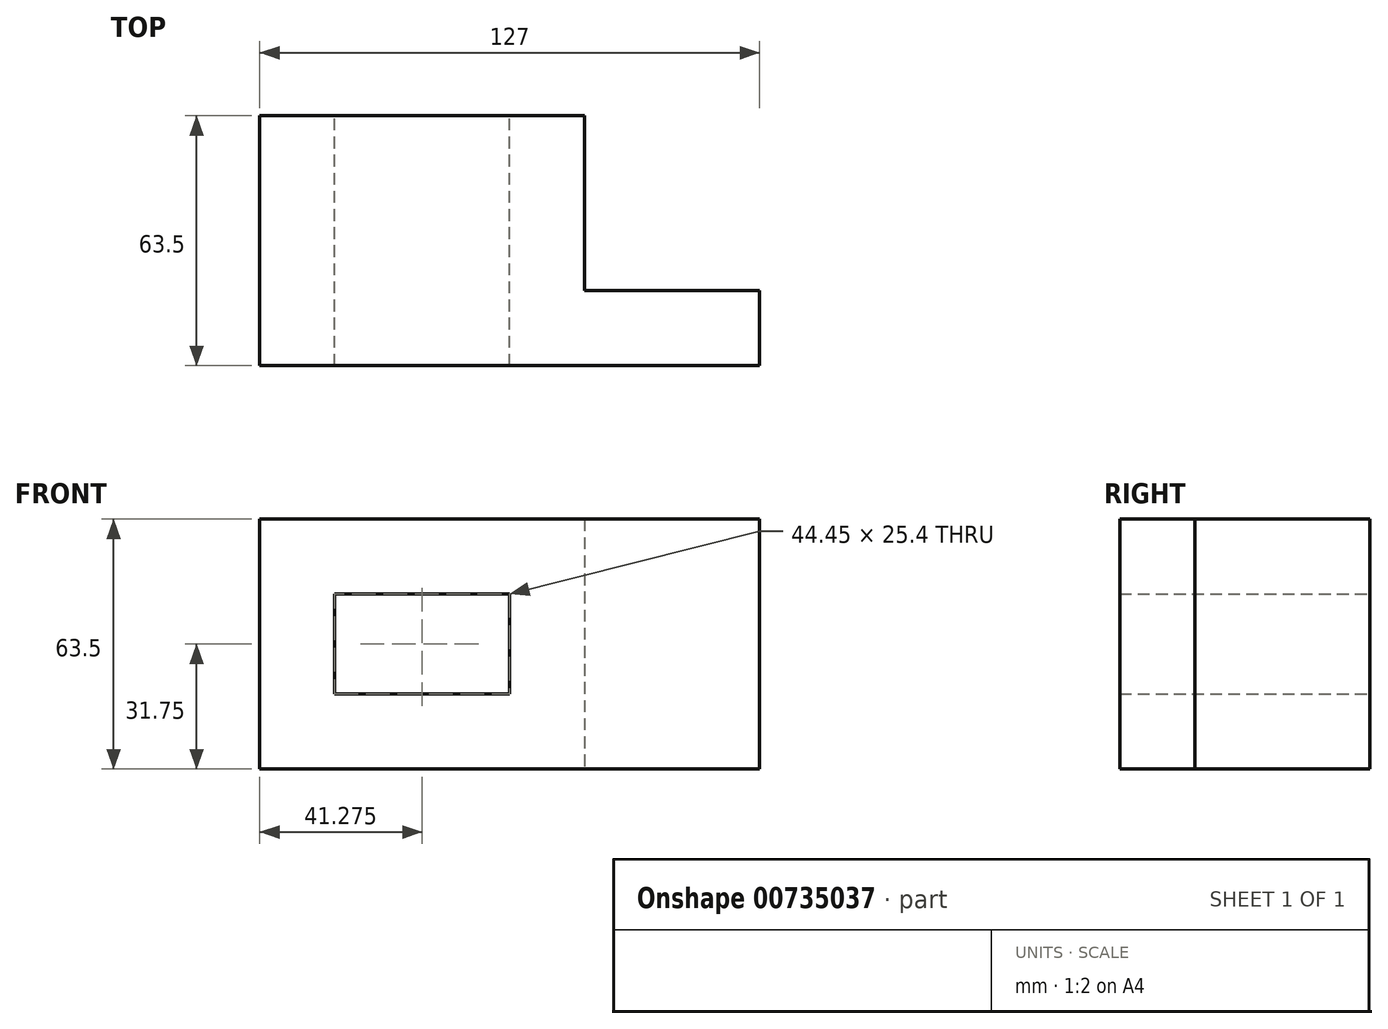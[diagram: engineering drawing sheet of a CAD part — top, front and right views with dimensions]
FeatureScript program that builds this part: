
annotation { "Feature Type Name" : "Feature", "Feature Type Description" : "" }
export const myFeature = defineFeature(function(context is Context, id is Id, definition is map)
    precondition{}
    {
        {
            var Q0;
            Q0=qCreatedBy(makeId("Front.planeOp"),FACE);
            var sketch = newSketch(context, id + "F0", { "sketchPlane" : qUnion([Q0])});
            skLineSegment(sketch, "E0", {"start": v(0, 0) * mm, "end": v(0, 63.5) * mm});
            skLineSegment(sketch, "E1", {"start": v(0, 63.5) * mm, "end": v(82.55, 63.5) * mm});
            skLineSegment(sketch, "E2", {"start": v(82.55, 63.5) * mm, "end": v(82.55, 0) * mm});
            skLineSegment(sketch, "E3", {"start": v(82.55, 0) * mm, "end": v(0, 0) * mm});
            skLineSegment(sketch, "E4", {"start": v(82.55, 63.5) * mm, "end": v(127, 63.5) * mm});
            skLineSegment(sketch, "E5", {"start": v(127, 63.5) * mm, "end": v(127, 0) * mm});
            skLineSegment(sketch, "E6", {"start": v(127, 0) * mm, "end": v(82.55, 0) * mm});
            skLineSegment(sketch, "E7", {"start": v(19.05, 19.05) * mm, "end": v(19.05, 44.45) * mm});
            skLineSegment(sketch, "E8", {"start": v(19.05, 44.45) * mm, "end": v(63.5, 44.45) * mm});
            skLineSegment(sketch, "E9", {"start": v(63.5, 44.45) * mm, "end": v(63.5, 19.05) * mm});
            skLineSegment(sketch, "E10", {"start": v(63.5, 19.05) * mm, "end": v(19.05, 19.05) * mm});
            skSolve(sketch);
        }
        {
            var Q0;
            Q0=makeQuery(id+"F0.imprint","IMPRINT",FACE,{"disambiguationData":[TD([[makeQuery(id+"F0.imprint","IMPRINT",EDGE,{"derivedFrom":sQuery(id+"F0.wireOp",EDGE,"E0")}),-1.0]])]});
            extrude(context, id + "F1", {"entities" : qUnion([Q0]), "depth" : 63.5 * mm, "offsetDistance" : 25.4 * mm});
        }
        {
            var Q0;
            Q0=makeQuery(id+"F1.opExtrude","CAP_FACE",FACE,{"disambiguationData":[OSD([sQuery(id+"F0.wireOp",EDGE,"E0"),sQuery(id+"F0.wireOp",EDGE,"E1"),sQuery(id+"F0.wireOp",EDGE,"E2"),sQuery(id+"F0.wireOp",EDGE,"E3"),sQuery(id+"F0.wireOp",EDGE,"E7"),sQuery(id+"F0.wireOp",EDGE,"E8"),sQuery(id+"F0.wireOp",EDGE,"E9"),sQuery(id+"F0.wireOp",EDGE,"E10")])],"isStart":false});
            var sketch = newSketch(context, id + "F2", { "sketchPlane" : qUnion([Q0])});
            skLineSegment(sketch, "E11", {"start": v(82.55, 63.5) * mm, "end": v(127, 63.5) * mm});
            skLineSegment(sketch, "E12", {"start": v(127, 63.5) * mm, "end": v(127, 0) * mm});
            skLineSegment(sketch, "E13", {"start": v(127, 0) * mm, "end": v(82.55, 0) * mm});
            skSolve(sketch);
        }
        {
            var Q0;
            Q0=makeQuery(id+"F2.imprint","IMPRINT",FACE,{"disambiguationData":[TD([[makeQuery(id+"F2.imprint","IMPRINT",EDGE,{"derivedFrom":sQuery(id+"F2.wireOp",EDGE,"E11")}),-1.0]])]});
            extrude(context, id + "F3", {"entities" : qUnion([Q0]), "operationType" : NewBodyOperationType.ADD, "oppositeDirection" : true, "depth" : 19.05 * mm, "offsetDistance" : 25.4 * mm});
        }
    });
